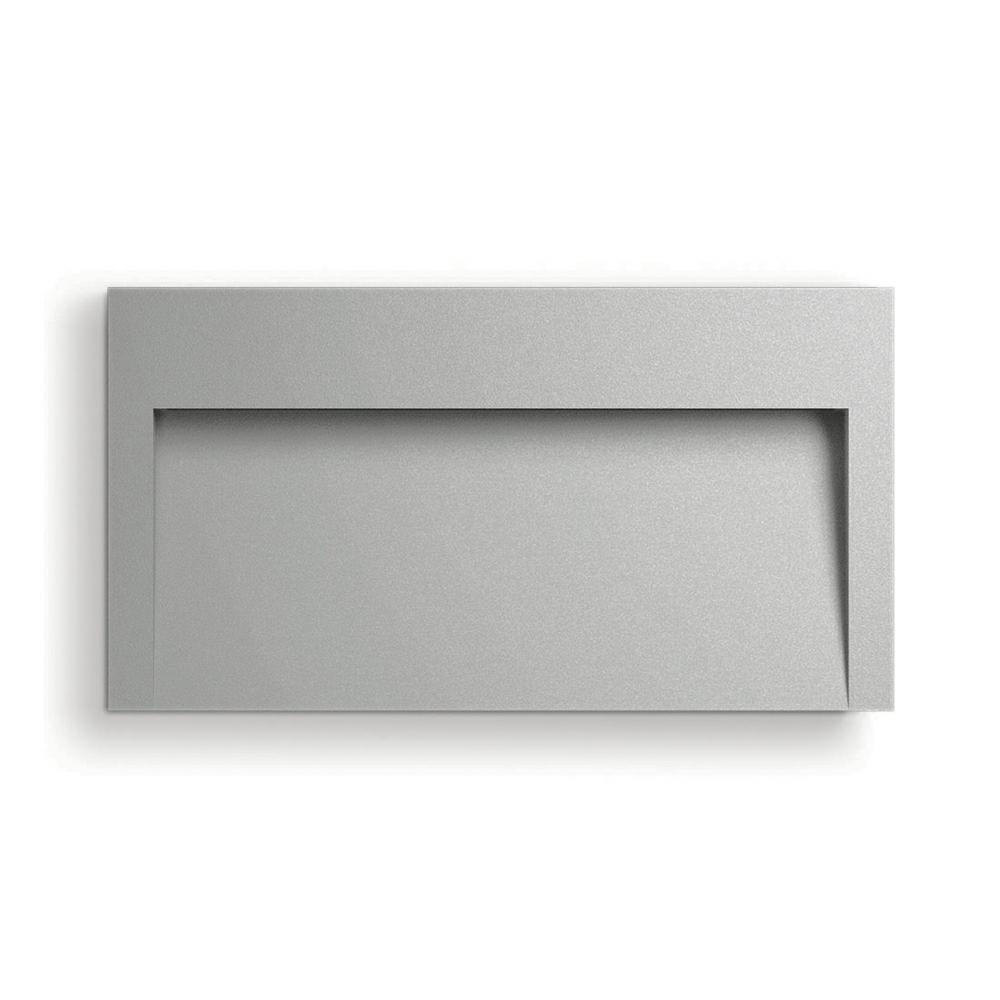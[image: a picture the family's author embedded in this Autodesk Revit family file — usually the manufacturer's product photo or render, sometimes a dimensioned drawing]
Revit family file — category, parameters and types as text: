
# Revit family: PLK_TEAM Medium Small PROVA
name_source: partatom
category: Apparecchi per illuminazione
revit_build: Autodesk Revit 2017 (Build: 20160225_1515(x64)
units: mm (PartAtom-declared; Revit-internal decimal feet)

## family parameters
Basato su piano di lavoro = No
Condiviso = No
Punto di calcolo locali = No
Quota connettore circolare = Usa diametro
Sempre verticale = Sì
Sorgente d'illuminazione = Sì
Taglio con vuoti quando caricato = No
Tipo di parte = Normale

## types (2) — shared parameters
Angolo inclinazione = 90.00°
CRI = >80
Cable Lenght = Cable input max. Ø 7 mm
Carico apparente = 0 VA
Colour Temperature = 3000 K
Commenti sul tipo = Paths, Ramps, Steps
Descrizione = Outdoor Lighting, Wall mounted
Diffuse Type = Polycarbonate
Dimmable = TRIAC
Emetti da larghezza rettangolo = 28 mm  [stored 0.0918635 ft]
Energy Efficiency Rating = A/A+/A++
Filtro dei colori = 16777215
Frequency = 50/60 Hz
Grey = PLK_Grey
IK Rating = IK08
IP Rating = IP65
Insulation Class = 1
LED Protection = Surge protection included
Lampada = LED
Light Source = PLK_Light Source
Luminaire Wattage = 8 W
Manufacturer Comment = IP68 connector included
Modello = TEAM
Mounting Type = Wall
Nota chiave = Other LED colors available on request
Power Supply Unit = Included
Product Documentation Link = http://www.platek.eu
Product Page URL = http://www.platek.eu
Produttore = PLATEK SRL
Rendi la forma visibile nel rendering = No
Supply Voltage = 230 V
Supply Voltage Max = 240 V
Supply Voltage Min = 220 V
URL = www.platek.eu
Variazione temperatura colore lampada con luminosità attenuata = <Nessuno>

## per-type parameters (varying)
| type | Beam Angle | Codice assieme | E | E30.5_90.5 | Emetti da lunghezza rettangolo | File diagramma fotometrico | Immagine tipo | L | L140_260 | Luminaire Luminous Flux | Luminaire Luminous Intensity | PLATEK Article Code | Product Dimension |
| 3480119_8W_LED_3000K_L260mm | 50.3° x 87° | 3080219.06(Grey);3080219.01(Black);3080219.02(White);3080219.07(Corten);3080219.08(Anthracite);3080219.09(Bronze) | 90.5 mm  [stored 0.296916 ft] | No | 230 mm | 3480219.IES | team_medium.jpg | 260 mm  [stored 0.853018 ft] | No | 894 lm | 725 cd | 3480219 | (L260xW30xH140)mm |
| 3480119_8W_LED_3000K_L140mm | 55.4°x82° | 3080119.06(Grey);3080119.01(Black);3080119.02(White);3080119.07(Corten);3080119.08(Anthracite);3080119.09(Bronze) | 30.5 mm  [stored 0.100066 ft] | Sì | 110 mm  [stored 0.360892 ft] | 3480119.IES | team_small.jpg | 140 mm  [stored 0.459318 ft] | Sì | 395 lm | 302 cd | 3480119 | (L140xW30xH140)mm |

note: [stored X ft] marks values corroborated as IEEE doubles in the binary element streams (Revit-internal decimal feet)
